# Revit family: Abmessungen emcoair KSW
name_source: partatom
category: Air Terminals
revit_build: Autodesk Revit 2017 (Build: 20190508_0315(x64)
units: mm (PartAtom-declared; Revit-internal decimal feet)

## family parameters
Always vertical = Yes
Cut with Voids When Loaded = No
Part Type = Normal
Room Calculation Point = No
Round Connector Dimension = Use Diameter
Shared = No
Work Plane-Based = No

## types (8) — shared parameters
10_Abstand Anschlusskastenoberseite / Stutzenmitte = 53 mm  [stored 0.173885 ft]
12_ Tiefe gesamt = 74 mm  [stored 0.242782 ft]
2_Höhe Anschlusskasten, gesamt = 280 mm  [stored 0.918635 ft]
8_Tiefe Anschlusskasten = 45 mm  [stored 0.147638 ft]
9_Länge Anschlussstutzen = 50 mm  [stored 0.164042 ft]
Product material = RAL 9016
t = 15 mm  [stored 0.0492126 ft]

## per-type parameters (varying)
| type | 11_ Durchmesser Zuluftstutzen / Abluftstutzen | 1_Breite Anschlusskasten, gesamt | 3_Breite Schlitzluftdurchlass ohne Endwinkel | 4_ Breite Schlitzluftdurchlass mit 2 Endwinkeln | 5_Höhe Schlitzluftdurchlass (ohne Auflageprofil) | 6_Höhe Schlitzluftdurchlass gesamt | 7_Abstand Zuluftstutzen / Abluftstutzen | Index | Index1 | Index2 | schlitzige Varianten |
| 800_2 | 98 mm  [stored 0.321522 ft] | 818 mm  [stored 2.68373 ft] | 800 mm  [stored 2.62467 ft] | 830 mm  [stored 2.7231 ft] | 73 mm  [stored 0.239501 ft] | 94 mm  [stored 0.308399 ft] | 408 mm | 1 | 1 | 1 | 15 mm  [stored 0.0492126 ft] |
| 800_1 | 78 mm  [stored 0.255906 ft] | 818 mm  [stored 2.68373 ft] | 800 mm  [stored 2.62467 ft] | 830 mm  [stored 2.7231 ft] | 41 mm  [stored 0.134514 ft] | 61 mm  [stored 0.200131 ft] | 408 mm | 0 | 0 | 1 | 0 mm  [stored 0 ft] |
| 1000_2 | 98 mm  [stored 0.321522 ft] | 1018 mm  [stored 3.3399 ft] | 1000 mm  [stored 3.28084 ft] | 1030 mm  [stored 3.37927 ft] | 73 mm  [stored 0.239501 ft] | 94 mm  [stored 0.308399 ft] | 508 mm | 1 | 1 | 2 | 15 mm  [stored 0.0492126 ft] |
| 1200_2 | 98 mm  [stored 0.321522 ft] | 1218 mm  [stored 3.99606 ft] | 1200 mm | 1230 mm  [stored 4.03543 ft] | 73 mm  [stored 0.239501 ft] | 94 mm  [stored 0.308399 ft] | 608 mm  [stored 1.99475 ft] | 1 | 1 | 3 | 15 mm  [stored 0.0492126 ft] |
| 1000_1 | 78 mm  [stored 0.255906 ft] | 1018 mm  [stored 3.3399 ft] | 1000 mm  [stored 3.28084 ft] | 1030 mm  [stored 3.37927 ft] | 41 mm  [stored 0.134514 ft] | 61 mm  [stored 0.200131 ft] | 508 mm | 0 | 0 | 2 | 0 mm  [stored 0 ft] |
| 1200_1 | 78 mm  [stored 0.255906 ft] | 1218 mm  [stored 3.99606 ft] | 1200 mm | 1230 mm  [stored 4.03543 ft] | 41 mm  [stored 0.134514 ft] | 61 mm  [stored 0.200131 ft] | 608 mm  [stored 1.99475 ft] | 0 | 0 | 3 | 0 mm  [stored 0 ft] |
| 500_2 | 98 mm  [stored 0.321522 ft] | 518 mm  [stored 1.69948 ft] | 500 mm  [stored 1.64042 ft] | 530 mm  [stored 1.73885 ft] | 73 mm  [stored 0.239501 ft] | 94 mm  [stored 0.308399 ft] | 0 mm  [stored 0 ft] | 1 | 1 | 0 | 15 mm  [stored 0.0492126 ft] |
| 500_1 | 78 mm  [stored 0.255906 ft] | 518 mm  [stored 1.69948 ft] | 500 mm  [stored 1.64042 ft] | 530 mm  [stored 1.73885 ft] | 41 mm  [stored 0.134514 ft] | 61 mm  [stored 0.200131 ft] | 0 mm  [stored 0 ft] | 0 | 0 | 0 | 0 mm  [stored 0 ft] |

note: [stored X ft] marks values corroborated as IEEE doubles in the binary element streams (Revit-internal decimal feet)

## geometry (parser evidence)
native form markers: Sweep x2
no freeform markers — native parametric forms only
